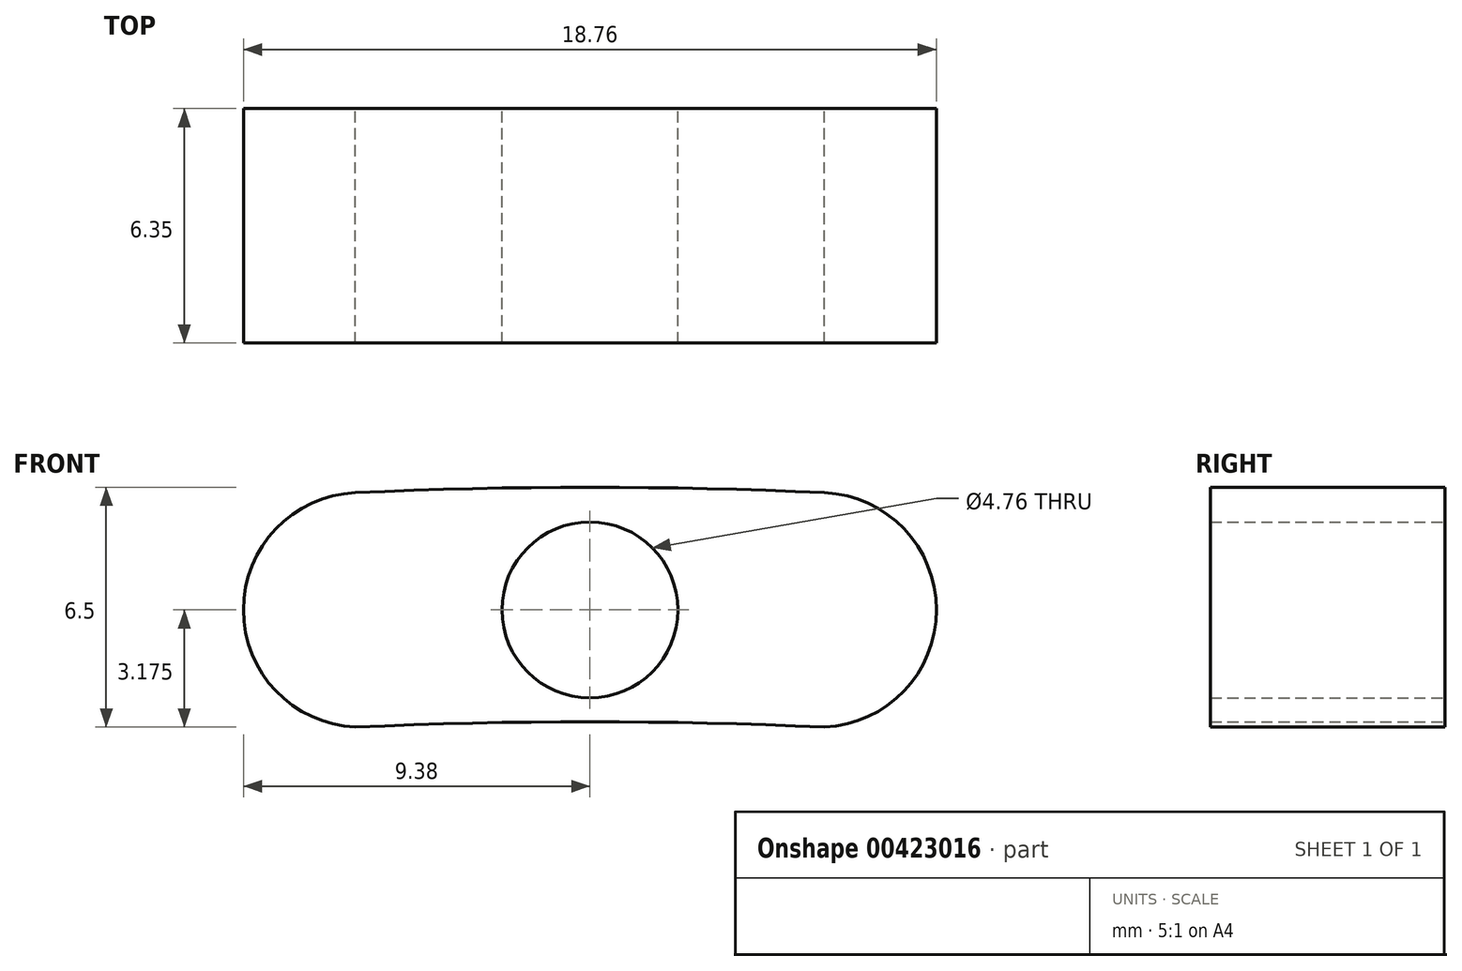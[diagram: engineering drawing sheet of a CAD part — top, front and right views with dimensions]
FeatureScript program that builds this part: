
annotation { "Feature Type Name" : "Feature", "Feature Type Description" : "" }
export const myFeature = defineFeature(function(context is Context, id is Id, definition is map)
    precondition{}
    {
        {
            var Q0;
            Q0=qCreatedBy(makeId("Front.planeOp"),FACE);
            var sketch = newSketch(context, id + "F0", { "sketchPlane" : qUnion([Q0])});
            skArc(sketch, "E0", {"start": v(6.35, 0) * mm, "mid": v(0, 0.15) * mm, "end": v(-6.35, 0) * mm});
            skArc(sketch, "E1", {"start": v(6.35, 6.35) * mm, "mid": v(0, 6.5) * mm, "end": v(-6.35, 6.35) * mm});
            skArc(sketch, "E2", {"start": v(-6.35, 6.35) * mm, "mid": v(-9.38, 3.17) * mm, "end": v(-6.35, 0) * mm});
            skArc(sketch, "E3", {"start": v(6.35, 6.35) * mm, "mid": v(9.38, 3.18) * mm, "end": v(6.35, 0) * mm});
            skCircle(sketch, "E4", {"center": v(0, 3.18) * mm, "radius": 2.38 * mm});
            skSolve(sketch);
        }
        {
            var Q0;
            Q0=qSketchRegion(id+"F0",true);
            extrude(context, id + "F1", {"entities" : qUnion([Q0]), "depth" : 6.35 * mm});
        }
    });
